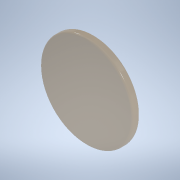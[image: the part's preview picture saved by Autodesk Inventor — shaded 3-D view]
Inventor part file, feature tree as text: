
AUTODESK INVENTOR PART (.ipt)
format: ipt  version: 2020 (Build 240168000, 168)  size: 112,128 bytes
history: native  units: mm
features: extrude x1, fillet x1, sketch x1
ambient origin geometry x8: Origin, YZ Plane, XZ Plane, XY Plane, X Axis, Y Axis, Z Axis, Center Point
bodies: Solid1 (feature_tree)
feature tree (3):
  extrude  "Extrusion1"  Depth=2.0mm TaperAngle=0.0deg
  fillet  "Fillet1"  Radius=0.5mm
  sketch  "Sketch1"  dims[d0=25.0mm d1=2.0mm d2=0.0mm d3=0.5mm]
